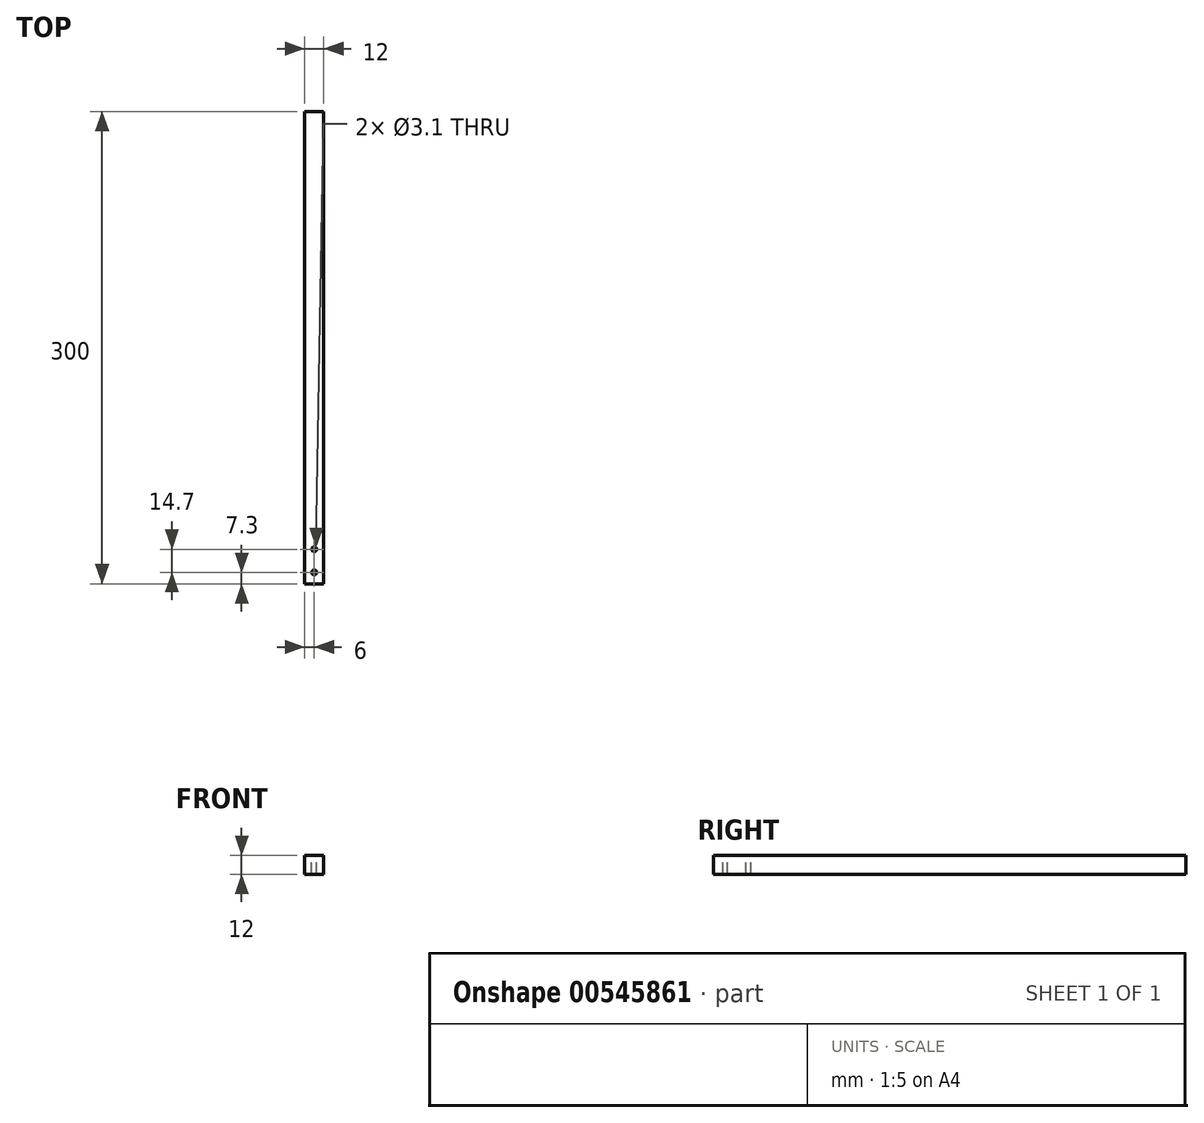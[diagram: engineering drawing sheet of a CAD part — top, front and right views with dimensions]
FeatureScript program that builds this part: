
annotation { "Feature Type Name" : "Feature", "Feature Type Description" : "" }
export const myFeature = defineFeature(function(context is Context, id is Id, definition is map)
    precondition{}
    {
        {
            var Q0;
            Q0=qCreatedBy(makeId("Front.planeOp"),FACE);
            var sketch = newSketch(context, id + "F0", { "sketchPlane" : qUnion([Q0])});
            skLineSegment(sketch, "E0.bottom", {"start": v(6, -6) * mm, "end": v(-6, -6) * mm});
            skLineSegment(sketch, "E0.top", {"start": v(6, 6) * mm, "end": v(-6, 6) * mm});
            skLineSegment(sketch, "E0.left", {"start": v(6, -6) * mm, "end": v(6, 6) * mm});
            skLineSegment(sketch, "E0.right", {"start": v(-6, -6) * mm, "end": v(-6, 6) * mm});
            skPoint(sketch, "E0.middle", {"position": v(0, 0) * mm});
            skSolve(sketch);
        }
        {
            var Q0;
            Q0 = qSketchRegion(id + "F0", true);
            extrude(context, id + "F1", {"entities" : qUnion([Q0]), "oppositeDirection" : true, "depth" : 300 * mm, "offsetDistance" : 25.4 * mm});
        }
        {
            var Q0;
            Q0=makeQuery(id+"F1.opExtrude","SWEPT_FACE",FACE,{"disambiguationData":[OSD([sQuery(id+"F0.wireOp",EDGE,"E0.top")])]});
            var sketch = newSketch(context, id + "F2", { "sketchPlane" : qUnion([Q0])});
            skCircle(sketch, "E1", {"center": v(0, 7.3) * mm, "radius": 1.55 * mm});
            skLineSegment(sketch, "E2", {"start": v(6, 0) * mm, "end": v(6, 7.3) * mm});
            skLineSegment(sketch, "E3", {"start": v(6, 7.3) * mm, "end": v(6, 22) * mm});
            skLineSegment(sketch, "E4", {"start": v(6, 22) * mm, "end": v(-6, 22) * mm});
            skLineSegment(sketch, "E5", {"start": v(6, 7.3) * mm, "end": v(-6, 7.3) * mm});
            skCircle(sketch, "E6", {"center": v(0, 22) * mm, "radius": 1.55 * mm});
            skSolve(sketch);
        }
        {
            var Q0;
            Q0 = qSketchRegion(id + "F2", true);
            extrude(context, id + "F3", {"entities" : qUnion([Q0]), "operationType" : NewBodyOperationType.REMOVE, "endBound" : BoundingType.THROUGH_ALL, "oppositeDirection" : true, "depth" : 25.4 * mm, "offsetDistance" : 25.4 * mm});
        }
    });
